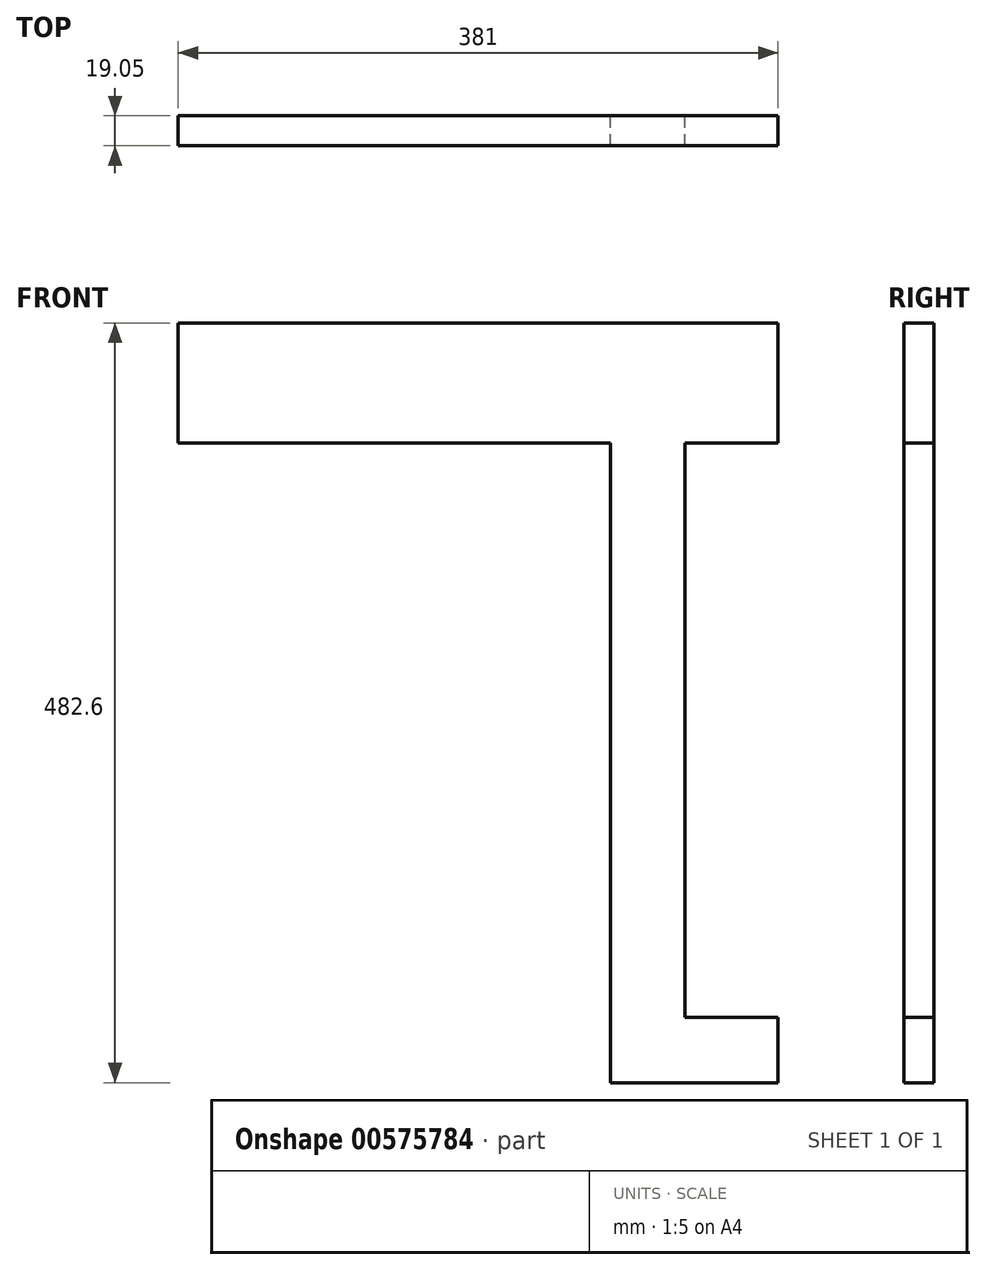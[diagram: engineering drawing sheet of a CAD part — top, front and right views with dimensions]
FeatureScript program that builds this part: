
annotation { "Feature Type Name" : "Feature", "Feature Type Description" : "" }
export const myFeature = defineFeature(function(context is Context, id is Id, definition is map)
    precondition{}
    {
        {
            var Q0;
            Q0=qCreatedBy(makeId("Front.planeOp"),FACE);
            var sketch = newSketch(context, id + "F0", { "sketchPlane" : qUnion([Q0])});
            skLineSegment(sketch, "E0.bottom", {"start": v(-185.45, 38.1) * mm, "end": v(195.55, 38.1) * mm});
            skLineSegment(sketch, "E0.left", {"start": v(-185.45, 38.1) * mm, "end": v(-185.45, -38.1) * mm});
            skLineSegment(sketch, "E0.right", {"start": v(195.55, 38.1) * mm, "end": v(195.55, -38.1) * mm});
            skPoint(sketch, "E0.middle", {"position": v(5.05, 0) * mm});
            skLineSegment(sketch, "E1", {"start": v(-185.45, -38.1) * mm, "end": v(89, -38.1) * mm});
            skLineSegment(sketch, "E2", {"start": v(89, -38.1) * mm, "end": v(89, -444.5) * mm});
            skLineSegment(sketch, "E3", {"start": v(89, -444.5) * mm, "end": v(195.55, -444.5) * mm});
            skLineSegment(sketch, "E4", {"start": v(195.55, -444.5) * mm, "end": v(195.55, -403.18) * mm});
            skLineSegment(sketch, "E5", {"start": v(195.55, -403.18) * mm, "end": v(136.36, -403.18) * mm});
            skLineSegment(sketch, "E6", {"start": v(136.36, -403.18) * mm, "end": v(136.36, -38.1) * mm});
            skLineSegment(sketch, "E7", {"start": v(136.36, -38.1) * mm, "end": v(195.55, -38.1) * mm});
            skSolve(sketch);
        }
        {
            var Q0;
            Q0 = qSketchRegion(id + "F0", true);
            extrude(context, id + "F1", {"entities" : qUnion([Q0]), "depth" : 19.05 * mm, "offsetDistance" : 25.4 * mm});
        }
    });
